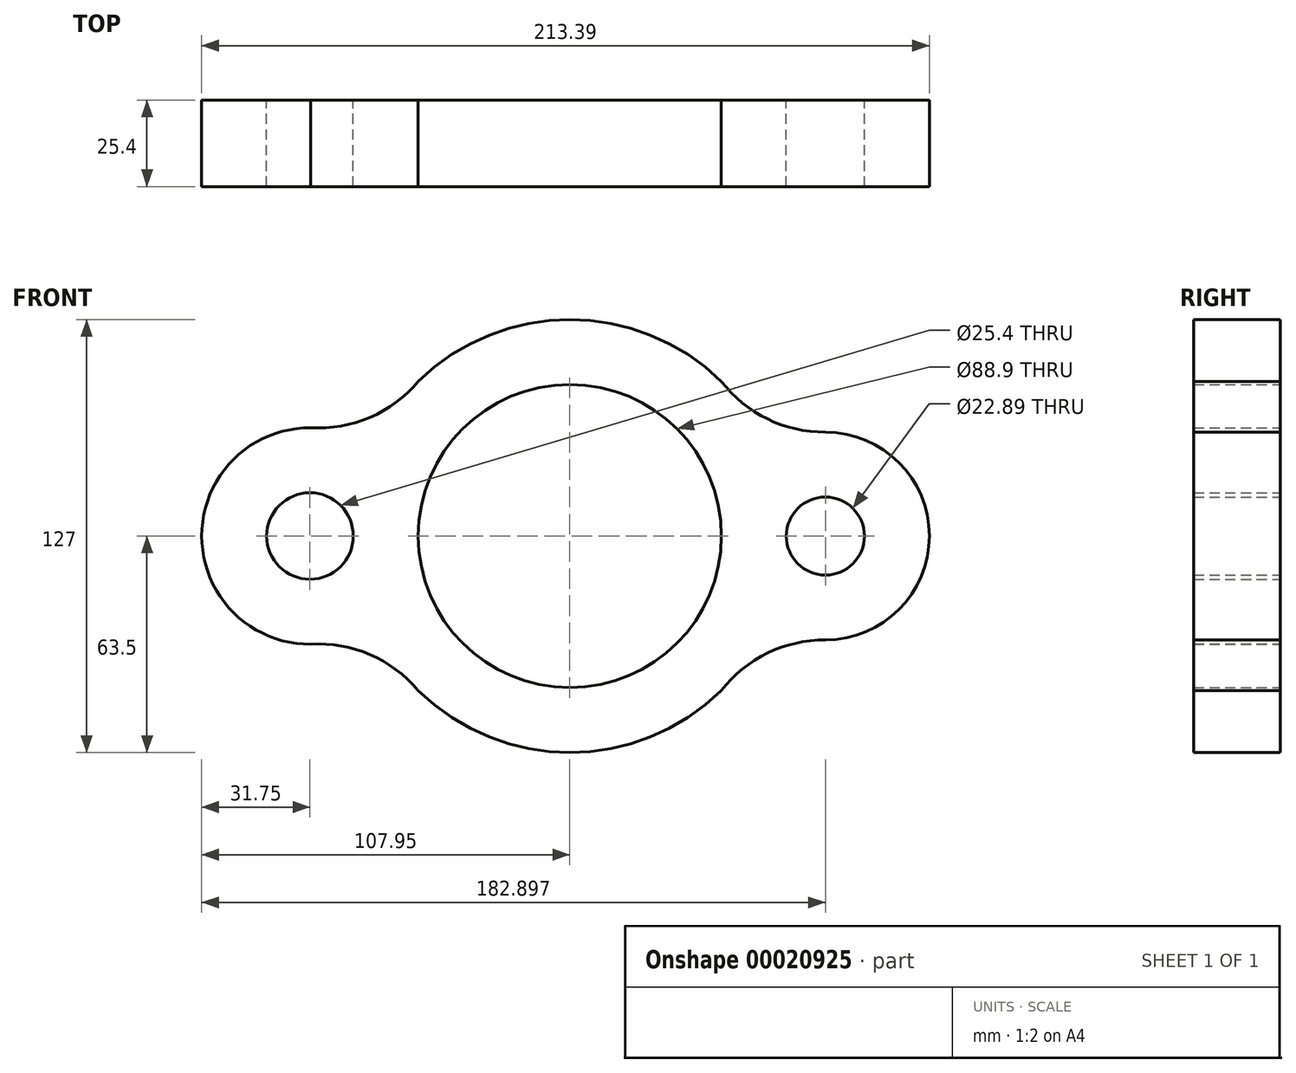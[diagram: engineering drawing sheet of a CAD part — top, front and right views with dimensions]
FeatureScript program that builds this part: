
annotation { "Feature Type Name" : "Feature", "Feature Type Description" : "" }
export const myFeature = defineFeature(function(context is Context, id is Id, definition is map)
    precondition{}
    {
        {
            var Q0;
            Q0=qCreatedBy(makeId("Front.planeOp"),FACE);
            var sketch = newSketch(context, id + "F0", { "sketchPlane" : qUnion([Q0])});
            skCircle(sketch, "E0", {"center": v(0, 0) * mm, "radius": 44.45 * mm});
            skArc(sketch, "E1", {"start": v(-47.7, -41.91) * mm, "mid": v(0.95, -63.5) * mm, "end": v(48.93, -40.47) * mm});
            skCircle(sketch, "E2", {"center": v(-76.2, 0) * mm, "radius": 12.7 * mm});
            skArc(sketch, "E3", {"start": v(-74.08, 31.68) * mm, "mid": v(-107.95, 0) * mm, "end": v(-74.08, -31.68) * mm});
            skCircle(sketch, "E4", {"center": v(74.95, 0) * mm, "radius": 11.45 * mm});
            skArc(sketch, "E5", {"start": v(74.67, -30.5) * mm, "mid": v(105.44, 0) * mm, "end": v(74.67, 30.5) * mm});
            skArc(sketch, "E6", {"start": v(-44.45, -45.35) * mm, "mid": v(-58.62, -34.78) * mm, "end": v(-76.03, -31.75) * mm});
            skArc(sketch, "E7", {"start": v(74.95, -30.5) * mm, "mid": v(57.95, -34.34) * mm, "end": v(44.45, -45.35) * mm});
            skArc(sketch, "E8", {"start": v(44.45, 45.35) * mm, "mid": v(57.95, 34.34) * mm, "end": v(74.95, 30.5) * mm});
            skArc(sketch, "E9.MirrorCS", {"start": v(-44.45, 45.35) * mm, "mid": v(-58.62, 34.78) * mm, "end": v(-76.03, 31.75) * mm});
            skArc(sketch, "E10.trimOffspring", {"start": v(48.93, 40.47) * mm, "mid": v(0.95, 63.5) * mm, "end": v(-47.7, 41.91) * mm});
            skPoint(sketch, "E11.start.orphan", {"position": v(44.45, 0) * mm});
            skSolve(sketch);
        }
        {
            var Q0;
            Q0=makeQuery(id+"F0.imprint","IMPRINT",FACE,{"disambiguationData":[TD([[makeQuery(id+"F0.imprint","IMPRINT",EDGE,{"derivedFrom":sQuery(id+"F0.wireOp",EDGE,"E0")}),-1.0]])]});
            extrude(context, id + "F1", {"entities" : qUnion([Q0]), "depth" : 25.4 * mm});
        }
    });
